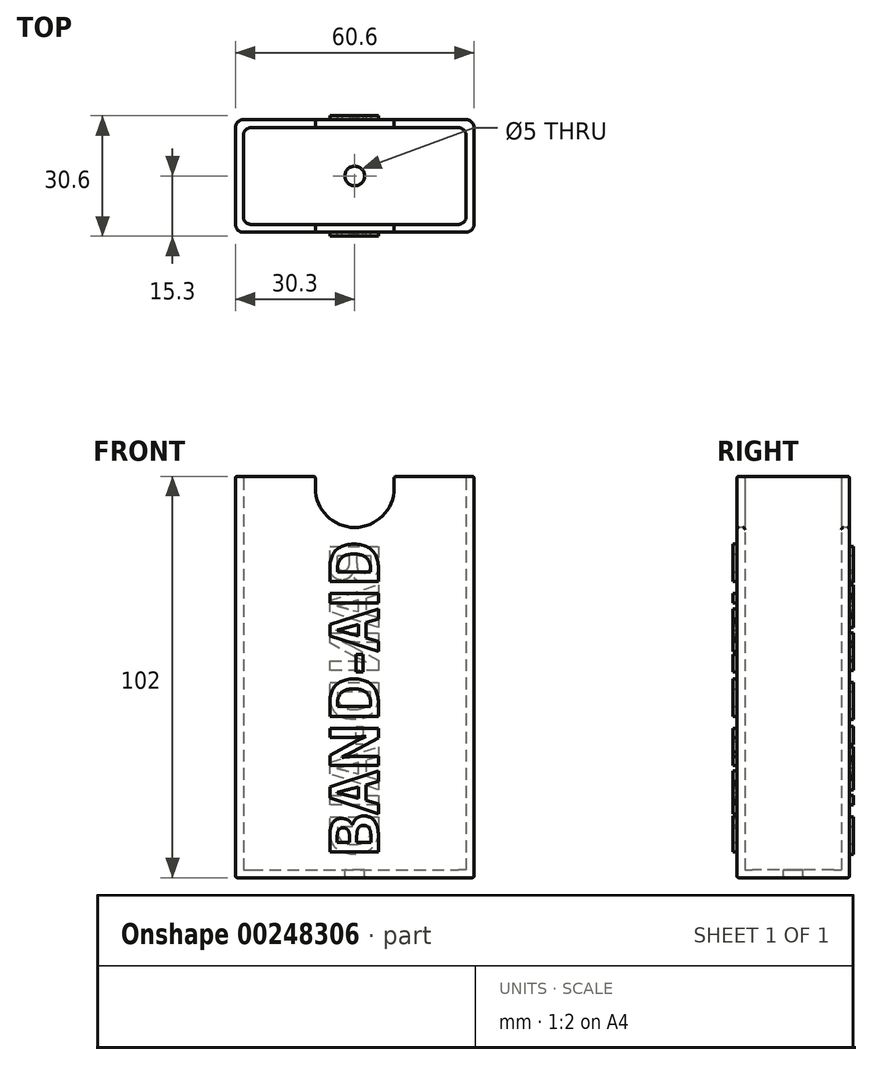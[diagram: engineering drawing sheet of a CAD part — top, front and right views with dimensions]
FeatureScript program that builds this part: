
annotation { "Feature Type Name" : "Feature", "Feature Type Description" : "" }
export const myFeature = defineFeature(function(context is Context, id is Id, definition is map)
    precondition{}
    {
        {
            var Q0;
            Q0=qCreatedBy(makeId("Top.planeOp"),FACE);
            var sketch = newSketch(context, id + "F0", { "sketchPlane" : qUnion([Q0])});
            skLineSegment(sketch, "E0.bottom", {"start": v(-26.3, 12.3) * mm, "end": v(26.3, 12.3) * mm});
            skLineSegment(sketch, "E0.top", {"start": v(-26.3, -12.3) * mm, "end": v(26.3, -12.3) * mm});
            skLineSegment(sketch, "E0.left", {"start": v(-28.3, 10.3) * mm, "end": v(-28.3, -10.3) * mm});
            skLineSegment(sketch, "E0.right", {"start": v(28.3, 10.3) * mm, "end": v(28.3, -10.3) * mm});
            skPoint(sketch, "E0.middle", {"position": v(0, 0) * mm});
            skPoint(sketch, "E1.visualSharp", {"position": v(-28.3, 12.3) * mm});
            skArc(sketch, "E1.filletArc", {"start": v(-26.3, 12.3) * mm, "mid": v(-27.71, 11.71) * mm, "end": v(-28.3, 10.3) * mm});
            skPoint(sketch, "E2.visualSharp", {"position": v(28.3, 12.3) * mm});
            skArc(sketch, "E2.filletArc", {"start": v(28.3, 10.3) * mm, "mid": v(27.71, 11.71) * mm, "end": v(26.3, 12.3) * mm});
            skPoint(sketch, "E3.visualSharp", {"position": v(28.3, -12.3) * mm});
            skArc(sketch, "E3.filletArc", {"start": v(26.3, -12.3) * mm, "mid": v(27.71, -11.71) * mm, "end": v(28.3, -10.3) * mm});
            skPoint(sketch, "E4.visualSharp", {"position": v(-28.3, -12.3) * mm});
            skArc(sketch, "E4.filletArc", {"start": v(-28.3, -10.3) * mm, "mid": v(-27.71, -11.71) * mm, "end": v(-26.3, -12.3) * mm});
            skLineSegment(sketch, "E5.bottom", {"start": v(-28.3, 14.3) * mm, "end": v(28.3, 14.3) * mm});
            skLineSegment(sketch, "E5.top", {"start": v(-28.3, -14.3) * mm, "end": v(28.3, -14.3) * mm});
            skLineSegment(sketch, "E5.left", {"start": v(-30.3, 12.3) * mm, "end": v(-30.3, -12.3) * mm});
            skLineSegment(sketch, "E5.right", {"start": v(30.3, 12.3) * mm, "end": v(30.3, -12.3) * mm});
            skPoint(sketch, "E6.visualSharp", {"position": v(-30.3, 14.3) * mm});
            skArc(sketch, "E6.filletArc", {"start": v(-28.3, 14.3) * mm, "mid": v(-29.71, 13.71) * mm, "end": v(-30.3, 12.3) * mm});
            skPoint(sketch, "E7.visualSharp", {"position": v(30.3, 14.3) * mm});
            skArc(sketch, "E7.filletArc", {"start": v(30.3, 12.3) * mm, "mid": v(29.71, 13.71) * mm, "end": v(28.3, 14.3) * mm});
            skPoint(sketch, "E8.visualSharp", {"position": v(30.3, -14.3) * mm});
            skArc(sketch, "E8.filletArc", {"start": v(28.3, -14.3) * mm, "mid": v(29.71, -13.71) * mm, "end": v(30.3, -12.3) * mm});
            skPoint(sketch, "E9.visualSharp", {"position": v(-30.3, -14.3) * mm});
            skArc(sketch, "E9.filletArc", {"start": v(-30.3, -12.3) * mm, "mid": v(-29.71, -13.71) * mm, "end": v(-28.3, -14.3) * mm});
            skSolve(sketch);
        }
        {
            var Q0;
            Q0 = qSketchRegion(id + "F0", true);
            extrude(context, id + "F1", {"entities" : qUnion([Q0]), "depth" : 100 * mm});
        }
        {
            var Q0;
            Q0=qCreatedBy(makeId("Top.planeOp"),FACE);
            var sketch = newSketch(context, id + "F2", { "sketchPlane" : qUnion([Q0])});
            skLineSegment(sketch, "E10.bottom", {"start": v(-28.3, -14.3) * mm, "end": v(28.3, -14.3) * mm});
            skLineSegment(sketch, "E10.top", {"start": v(-28.3, 14.3) * mm, "end": v(28.3, 14.3) * mm});
            skLineSegment(sketch, "E10.left", {"start": v(-30.3, -12.3) * mm, "end": v(-30.3, 12.3) * mm});
            skLineSegment(sketch, "E10.right", {"start": v(30.3, -12.3) * mm, "end": v(30.3, 12.3) * mm});
            skPoint(sketch, "E10.middle", {"position": v(0, 0) * mm});
            skPoint(sketch, "E11.visualSharp", {"position": v(-30.3, -14.3) * mm});
            skArc(sketch, "E11.filletArc", {"start": v(-30.3, -12.3) * mm, "mid": v(-29.71, -13.71) * mm, "end": v(-28.3, -14.3) * mm});
            skPoint(sketch, "E12.visualSharp", {"position": v(30.3, -14.3) * mm});
            skArc(sketch, "E12.filletArc", {"start": v(28.3, -14.3) * mm, "mid": v(29.71, -13.71) * mm, "end": v(30.3, -12.3) * mm});
            skPoint(sketch, "E13.visualSharp", {"position": v(30.3, 14.3) * mm});
            skArc(sketch, "E13.filletArc", {"start": v(30.3, 12.3) * mm, "mid": v(29.71, 13.71) * mm, "end": v(28.3, 14.3) * mm});
            skPoint(sketch, "E14.visualSharp", {"position": v(-30.3, 14.3) * mm});
            skArc(sketch, "E14.filletArc", {"start": v(-28.3, 14.3) * mm, "mid": v(-29.71, 13.71) * mm, "end": v(-30.3, 12.3) * mm});
            skCircle(sketch, "E15", {"center": v(0, 0) * mm, "radius": 2.5 * mm});
            skSolve(sketch);
        }
        {
            var Q0;
            Q0 = qSketchRegion(id + "F2", true);
            extrude(context, id + "F3", {"entities" : qUnion([Q0]), "operationType" : NewBodyOperationType.ADD, "oppositeDirection" : true, "depth" : 2 * mm});
        }
        {
            var Q0;
            Q0=makeQuery(id+"F3.boolean.opBoolean","MERGE",FACE,{"derivedFrom":[makeQuery(id+"F1.opExtrude","SWEPT_FACE",FACE,{"disambiguationData":[OSD([sQuery(id+"F0.wireOp",EDGE,"E5.top")])]}),makeQuery(id+"F3.opExtrude","SWEPT_FACE",FACE,{"disambiguationData":[OSD([sQuery(id+"F2.wireOp",EDGE,"E10.bottom")])]})]});
            var sketch = newSketch(context, id + "F4", { "sketchPlane" : qUnion([Q0])});
            skText(sketch, "E16", { "text": "BAND-AID", "fontName": "NotoSansCJKjp-Bold.otf"});
            const initialGuessF4  = {"E16": [0.006, 0.003, 0, 1, 0.012]};
            skSetInitialGuess(sketch, initialGuessF4);
            skSolve(sketch);
        }
        {
            var Q0;
            Q0 = qSketchRegion(id + "F4", true);
            extrude(context, id + "F5", {"entities" : qUnion([Q0]), "operationType" : NewBodyOperationType.ADD, "depth" : 1 * mm});
        }
        {
            var Q0;
            Q0=makeQuery(id+"F3.boolean.opBoolean","MERGE",FACE,{"derivedFrom":[makeQuery(id+"F1.opExtrude","SWEPT_FACE",FACE,{"disambiguationData":[OSD([sQuery(id+"F0.wireOp",EDGE,"E5.bottom")])]}),makeQuery(id+"F3.opExtrude","SWEPT_FACE",FACE,{"disambiguationData":[OSD([sQuery(id+"F2.wireOp",EDGE,"E10.top")])]})]});
            var sketch = newSketch(context, id + "F6", { "sketchPlane" : qUnion([Q0])});
            skText(sketch, "E17", { "text": "BAND-AID", "fontName": "NotoSansCJKjp-Bold.otf"});
            const initialGuessF6  = {"E17": [-0.006, 0.08371, 0, -1, 0.012]};
            skSetInitialGuess(sketch, initialGuessF6);
            skSolve(sketch);
        }
        {
            var Q0;
            Q0 = qSketchRegion(id + "F6", true);
            extrude(context, id + "F7", {"entities" : qUnion([Q0]), "operationType" : NewBodyOperationType.ADD, "depth" : 1 * mm});
        }
        {
            var Q0;
            Q0=qCreatedBy(makeId("Front.planeOp"),FACE);
            var sketch = newSketch(context, id + "F8", { "sketchPlane" : qUnion([Q0])});
            skArc(sketch, "E18", {"start": v(-10, 97) * mm, "mid": v(0, 87) * mm, "end": v(10, 97) * mm});
            skLineSegment(sketch, "E19", {"start": v(10, 97) * mm, "end": v(10, 100) * mm});
            skLineSegment(sketch, "E20", {"start": v(10, 100) * mm, "end": v(-10, 100) * mm});
            skLineSegment(sketch, "E21", {"start": v(-10, 100) * mm, "end": v(-10, 97) * mm});
            skSolve(sketch);
        }
        {
            var Q0;
            Q0 = qSketchRegion(id + "F8", true);
            extrude(context, id + "F9", {"entities" : qUnion([Q0]), "operationType" : NewBodyOperationType.REMOVE, "endBound" : BoundingType.SYMMETRIC, "oppositeDirection" : true, "depth" : 70 * mm});
        }
        {
            var Q0;
            Q0=makeQuery(id+"F3.opExtrude","CAP_FACE",FACE,{"disambiguationData":[OSD([sQuery(id+"F2.wireOp",EDGE,"E10.bottom"),sQuery(id+"F2.wireOp",EDGE,"E10.top"),sQuery(id+"F2.wireOp",EDGE,"E10.left"),sQuery(id+"F2.wireOp",EDGE,"E10.right"),sQuery(id+"F2.wireOp",EDGE,"E11.filletArc"),sQuery(id+"F2.wireOp",EDGE,"E12.filletArc"),sQuery(id+"F2.wireOp",EDGE,"E13.filletArc"),sQuery(id+"F2.wireOp",EDGE,"E14.filletArc"),sQuery(id+"F2.wireOp",EDGE,"E15")])],"isStart":false});
            var Q1;
            Q1=makeQuery(id+"F1.opExtrude","CAP_FACE",FACE,{"disambiguationData":[OSD([sQuery(id+"F0.wireOp",EDGE,"E0.bottom"),sQuery(id+"F0.wireOp",EDGE,"E0.top"),sQuery(id+"F0.wireOp",EDGE,"E0.left"),sQuery(id+"F0.wireOp",EDGE,"E0.right"),sQuery(id+"F0.wireOp",EDGE,"E1.filletArc"),sQuery(id+"F0.wireOp",EDGE,"E2.filletArc"),sQuery(id+"F0.wireOp",EDGE,"E3.filletArc"),sQuery(id+"F0.wireOp",EDGE,"E4.filletArc"),sQuery(id+"F0.wireOp",EDGE,"E5.bottom"),sQuery(id+"F0.wireOp",EDGE,"E5.top"),sQuery(id+"F0.wireOp",EDGE,"E5.left"),sQuery(id+"F0.wireOp",EDGE,"E5.right"),sQuery(id+"F0.wireOp",EDGE,"E6.filletArc"),sQuery(id+"F0.wireOp",EDGE,"E7.filletArc"),sQuery(id+"F0.wireOp",EDGE,"E8.filletArc"),sQuery(id+"F0.wireOp",EDGE,"E9.filletArc")])],"isStart":false});
            var Q2;
            Q2=makeQuery(id+"F9.boolean.opBoolean","COPY",FACE,{"disambiguationData":[TD([makeQuery(id+"F1.opExtrude","SWEPT_FACE",FACE,{"disambiguationData":[OSD([sQuery(id+"F0.wireOp",EDGE,"E0.top")])]})])],"derivedFrom":makeQuery(id+"F9.opExtrude","SWEPT_FACE",FACE,{"disambiguationData":[OSD([sQuery(id+"F8.wireOp",EDGE,"E18")])]})});
            var Q3;
            {var subQ1=sQuery(id+"F0.wireOp",EDGE,"E0.top");Q3=makeQuery(id+"F9.boolean.opBoolean","COPY",FACE,{"disambiguationData":[TD([makeQuery(id+"F1.opExtrude","SWEPT_FACE",FACE,{"disambiguationData":[OSD([subQ1])]})])],"derivedFrom":makeQuery(id+"F9.opExtrude","SWEPT_FACE",FACE,{"disambiguationData":[OSD([sQuery(id+"F8.wireOp",EDGE,"E21")])]})});}
            var Q4;
            {var subQ1=sQuery(id+"F0.wireOp",EDGE,"E0.bottom");Q4=makeQuery(id+"F9.boolean.opBoolean","COPY",FACE,{"disambiguationData":[TD([makeQuery(id+"F1.opExtrude","SWEPT_FACE",FACE,{"disambiguationData":[OSD([subQ1])]})])],"derivedFrom":makeQuery(id+"F9.opExtrude","SWEPT_FACE",FACE,{"disambiguationData":[OSD([sQuery(id+"F8.wireOp",EDGE,"E19")])]})});}
            var Q5;
            Q5=makeQuery(id+"F9.boolean.opBoolean","COPY",FACE,{"disambiguationData":[TD([makeQuery(id+"F1.opExtrude","SWEPT_FACE",FACE,{"disambiguationData":[OSD([sQuery(id+"F0.wireOp",EDGE,"E0.bottom")])]})])],"derivedFrom":makeQuery(id+"F9.opExtrude","SWEPT_FACE",FACE,{"disambiguationData":[OSD([sQuery(id+"F8.wireOp",EDGE,"E18")])]})});
            fillet(context, id + "F10", {"entities" : qUnion([Q0, Q1, Q2, Q3, Q4, Q5]), "radius" : .5 * mm, "tangentPropagation" : true, "allowEdgeOverflow" : false});
        }
    });
